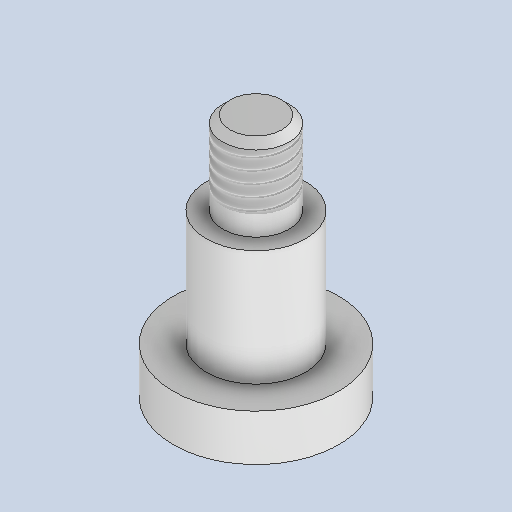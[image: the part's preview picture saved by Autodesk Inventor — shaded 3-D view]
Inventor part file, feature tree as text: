
AUTODESK INVENTOR PART (.ipt)
format: ipt  version: 2024.2 (Build 282272000, 272)  size: 290,304 bytes
history: native  units: mm
features: sketch x2, revolve x1, thread x1, extrude x1, chamfer x1
ambient origin geometry x8: Origin, YZ Plane, XZ Plane, XY Plane, X Axis, Y Axis, Z Axis, Center Point
bodies: Solid1 (feature_tree)
feature tree (6):
  revolve  "Revolution1"  [1 undecoded]
  thread  "Thread1"  [1 undecoded]
  extrude  "Extrusion1"  Depth=7.0mm
  chamfer  "Chamfer1"  Distance=2.8mm
  sketch  "Sketch1"  dims[d0=10.0mm d1=6.0mm d2=4.0mm]
  sketch  "Sketch2"  dims[d3=5.0mm d4=7.0mm d5=2.8mm d6=90.0deg d7=6.0mm d8=1.2mm d9=2.5mm d10=2.0mm d11=0.0mm d12=0.43mm d13=2.0mm d14=45.0deg]
note: 2 required parameter values undecoded (feature->parameter linkage not recoverable at this tier; creation-order binding heuristic only, values carry confidence <= 0.55)